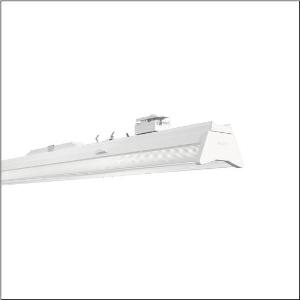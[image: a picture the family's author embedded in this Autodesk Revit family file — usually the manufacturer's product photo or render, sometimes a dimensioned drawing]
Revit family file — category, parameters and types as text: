
# Revit family: licross_r__21_performance_mo_52td16dn46xg_ca4f
name_source: partatom
category: Lighting Fixtures
units: mm (PartAtom-declared; Revit-internal decimal feet)

## family parameters
Cut with Voids When Loaded = No
Host = Face
Light Source = No
Part Type = Normal
Room Calculation Point = No
Round Connector Dimension = Use Diameter
Shared = No

## types (1)
- --- (1 x LED, 6000 lm, 32.7 W, 4000K)
    Apparent Load = 33 VA
    CIE Flux Codes = 66 88 96 79 100
    Color Rendering = 80
    Color Temperature = 4000K
    Default Elevation = 1800 mm
    Description = Licross® 21 Performance MO, luminaire insert, of sheet steel, galvanised, coil coated, white, length: 1.500mm, width: 120mm, height: 123mm, LED rated luminous flux: 6.000lm, light colour: 840, control gear: DALI 2, with plug, 5-pole, with phase selection, mains connection: 220..240V, AC, 50/60Hz, rated input power: 33W, halogen-free wiring, primary light control with lens, of plastic, primary optical cover: cover, of PMMA, light emission: direct/indirect distribution, primary light characteristic: symmetric, protection rating (complete): IP54, insulation class (complete): insulation class I (protective earthing), certification: CE, ENEC, VDE, UKCA, protection symbol: D if used in an environment with non-conductive dust loads with corresponding accessories, impact resistance: IK06, permissible ambient temperature for indoor applications: -25..+45°C, corresponds to IFS (International Featured Standards) requirements for safety and quality in the food industry, reducing of maximum allowable ambient temperature of 5°C with ceiling mounting, LABS conformity tested according to VDMA 24364:2018-05, packaging unit: 1 piece
    Height = 114 mm
    Lamp = 1 x LED
    Lamp Light Flux = 6000 lm
    Lamp Power = 32.7 W
    Lamp count = 1
    Length = 1500 mm
    Luminous efficacy = 183 lm/W
    Manufacturer = Siteco
    ModVariant = No
    Model = 52TD16DN46XG
    Mounting Place = Ceiling
    Mounting Type = Pendant
    Number of Poles = 1
    OnlyDefault = Yes
    Power Factor = 1
    Product Name = Licross® 21 Performance MO
    Product group = luminaire insert
    ProductGroupID = 901
    Protection Class = Protection class I
    Protection Degree = IP 54
    RLX_Detail_Level = 1
    RLX_Emergency_Light_Flux = 0 lm
    RLX_Emergency_Type = 0
    RLX_Emergency_Type_DB = No
    RlxData = <blob elided: 33689 chars, md5=d0b80003>
    Socket = socket
    Standby Power = 0 W
    System Light Flux = 6000 lm
    System Power = 33 W
    Type Comments = factory setting: luminous flux: 100 % | dim-lin: 254 | 222 mA
    Type Image = l_1256138.jpg
    URL = http://relux.com
    VarID = @adj_078881
    Voltage = 0 V
    Weight = 0.00 kg
    Width = 120 mm

## geometry (parser evidence)
native form markers: Blend x4, Sweep x10
no freeform markers — native parametric forms only
